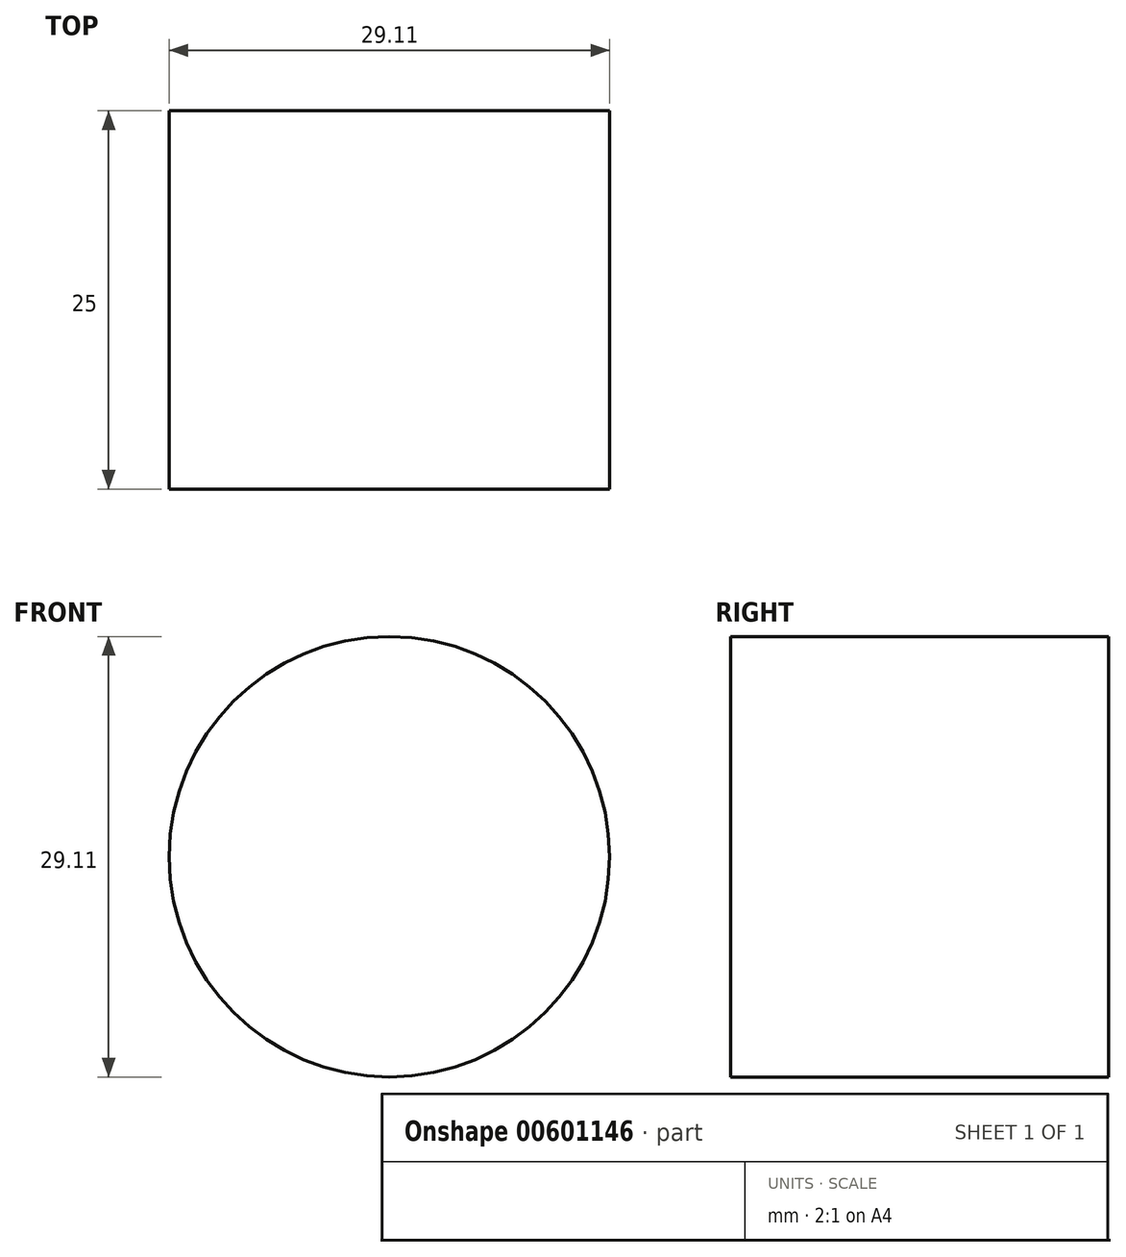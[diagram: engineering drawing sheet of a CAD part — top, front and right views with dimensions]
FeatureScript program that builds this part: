
annotation { "Feature Type Name" : "Feature", "Feature Type Description" : "" }
export const myFeature = defineFeature(function(context is Context, id is Id, definition is map)
    precondition{}
    {
        {
            var Q0;
            Q0=qCreatedBy(makeId("Front.planeOp"),FACE);
            var sketch = newSketch(context, id + "F0", { "sketchPlane" : qUnion([Q0])});
            skCircle(sketch, "E0", {"center": v(-143.68, 39.6) * mm, "radius": 14.55 * mm});
            skSolve(sketch);
        }
        {
            var Q0;
            Q0 = qSketchRegion(id + "F0", true);
            extrude(context, id + "F1", {"entities" : qUnion([Q0]), "depth" : 25 * mm, "offsetDistance" : 25 * mm});
        }
    });
